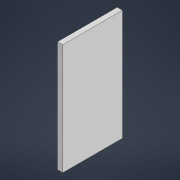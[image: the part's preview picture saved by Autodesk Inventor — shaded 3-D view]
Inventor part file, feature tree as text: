
AUTODESK INVENTOR PART (.ipt)
format: ipt  version: 2022 (Build 260153000, 153)  size: 85,504 bytes
history: native  units: mm
features: other x1, extrude x1, sketch x1
ambient origin geometry x8: Origin, YZ Plane, XZ Plane, XY Plane, X Axis, Y Axis, Z Axis, Center Point
bodies: Body1 (feature_tree)
feature tree (3):
  other  "Твердое тело1"
  extrude  "Выдавливание1"  Depth=470.0mm
  sketch  "Эскиз1"
